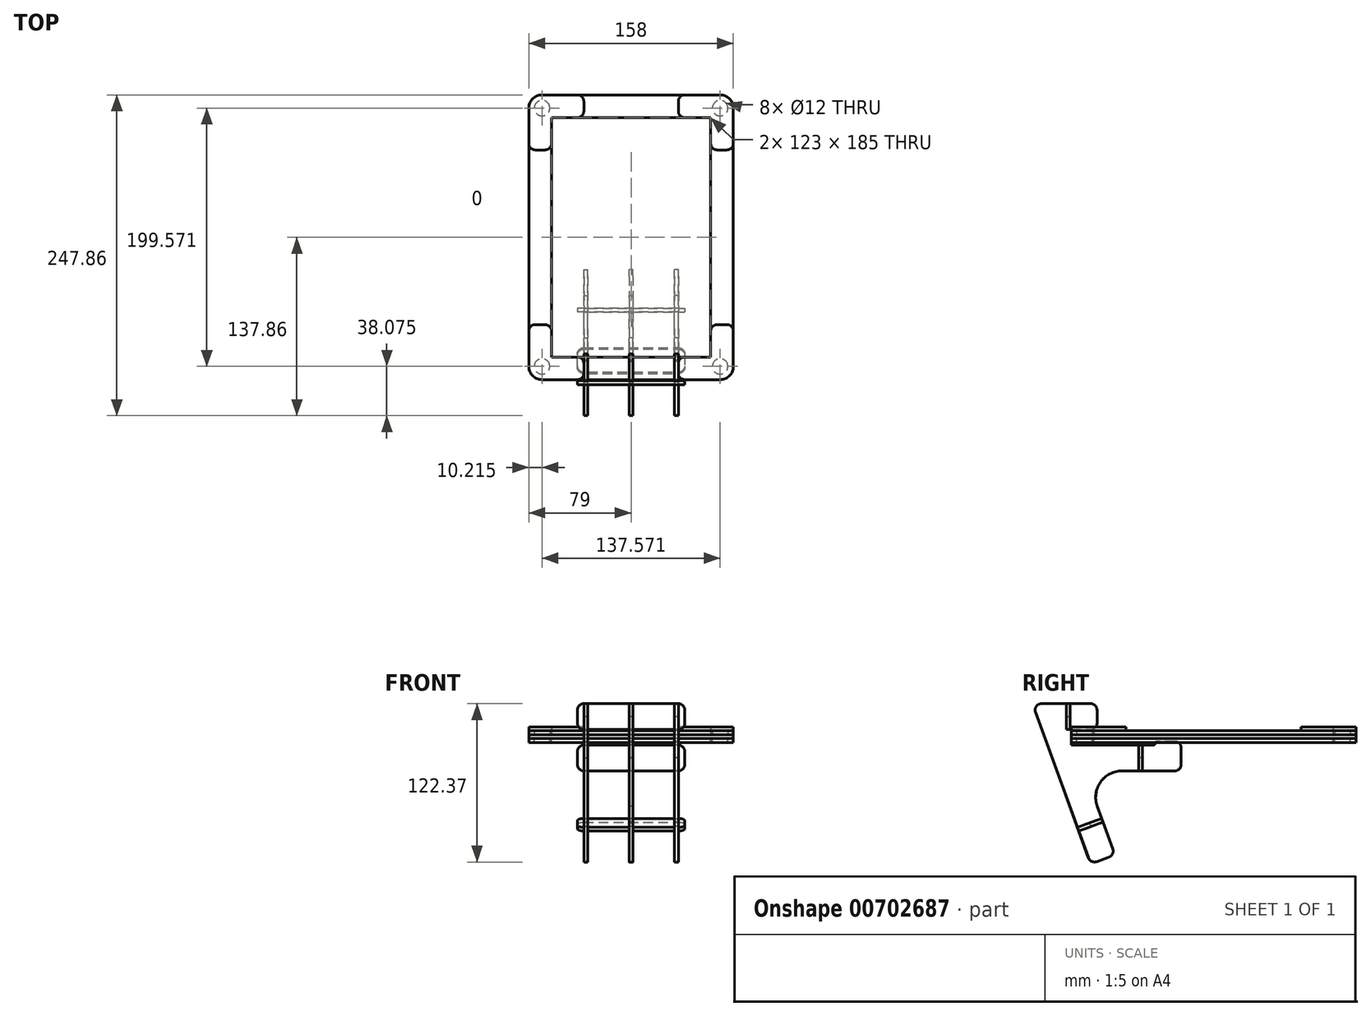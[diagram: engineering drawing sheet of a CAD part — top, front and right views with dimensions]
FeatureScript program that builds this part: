
annotation { "Feature Type Name" : "Feature", "Feature Type Description" : "" }
export const myFeature = defineFeature(function(context is Context, id is Id, definition is map)
    precondition{}
    {
        {
            var Q0;
            Q0=qCreatedBy(makeId("Top.planeOp"),FACE);
            var sketch = newSketch(context, id + "F0", { "sketchPlane" : qUnion([Q0])});
            skLineSegment(sketch, "E0.bottom", {"start": v(69, -110) * mm, "end": v(-69, -110) * mm});
            skLineSegment(sketch, "E0.top", {"start": v(69, 110) * mm, "end": v(-69, 110) * mm});
            skLineSegment(sketch, "E0.left", {"start": v(79, -100) * mm, "end": v(79, 100) * mm});
            skLineSegment(sketch, "E0.right", {"start": v(-79, -100) * mm, "end": v(-79, 100) * mm});
            skPoint(sketch, "E0.middle", {"position": v(0, 0) * mm});
            skPoint(sketch, "E1.visualSharp", {"position": v(-79, 110) * mm});
            skArc(sketch, "E1.filletArc", {"start": v(-69, 110) * mm, "mid": v(-76.07, 107.07) * mm, "end": v(-79, 100) * mm});
            skPoint(sketch, "E2.visualSharp", {"position": v(79, 110) * mm});
            skArc(sketch, "E2.filletArc", {"start": v(79, 100) * mm, "mid": v(76.07, 107.07) * mm, "end": v(69, 110) * mm});
            skPoint(sketch, "E3.visualSharp", {"position": v(79, -110) * mm});
            skArc(sketch, "E3.filletArc", {"start": v(69, -110) * mm, "mid": v(76.07, -107.07) * mm, "end": v(79, -100) * mm});
            skPoint(sketch, "E4.visualSharp", {"position": v(-79, -110) * mm});
            skArc(sketch, "E4.filletArc", {"start": v(-79, -100) * mm, "mid": v(-76.07, -107.07) * mm, "end": v(-69, -110) * mm});
            skSolve(sketch);
        }
        {
            var Q0;
            Q0 = qSketchRegion(id + "F0", true);
            extrude(context, id + "F1", {"entities" : qUnion([Q0]), "depth" : 3 * mm, "offsetDistance" : 25 * mm});
        }
        {
            var Q0;
            Q0=makeQuery(id+"F1.opExtrude","CAP_FACE",FACE,{"disambiguationData":[OSD([sQuery(id+"F0.wireOp",EDGE,"E0.bottom"),sQuery(id+"F0.wireOp",EDGE,"E0.top"),sQuery(id+"F0.wireOp",EDGE,"E0.left"),sQuery(id+"F0.wireOp",EDGE,"E0.right"),sQuery(id+"F0.wireOp",EDGE,"E1.filletArc"),sQuery(id+"F0.wireOp",EDGE,"E2.filletArc"),sQuery(id+"F0.wireOp",EDGE,"E3.filletArc"),sQuery(id+"F0.wireOp",EDGE,"E4.filletArc"),sQuery(id+"F0.wireOp",EDGE,"Dd5P2XuF-zcKf-sQkH-Ib6c-oR9rnRoDZ1EX.bottom"),sQuery(id+"F0.wireOp",EDGE,"Dd5P2XuF-zcKf-sQkH-Ib6c-oR9rnRoDZ1EX.top"),sQuery(id+"F0.wireOp",EDGE,"Dd5P2XuF-zcKf-sQkH-Ib6c-oR9rnRoDZ1EX.left"),sQuery(id+"F0.wireOp",EDGE,"Dd5P2XuF-zcKf-sQkH-Ib6c-oR9rnRoDZ1EX.right")])],"isStart":false});
            cPlane(context, id + "F2", {"entities" : qUnion([Q0]), "cplaneType" : CPlaneType.OFFSET, "offset" : 0 * mm, "width" : 150 * mm, "height" : 150 * mm});
        }
        {
            var Q0;
            Q0=qCreatedBy(id+"F2.planeOp",FACE);
            var sketch = newSketch(context, id + "F3", { "sketchPlane" : qUnion([Q0])});
            skLineSegment(sketch, "E5.bottom", {"start": v(69, -110) * mm, "end": v(-69, -110) * mm});
            skLineSegment(sketch, "E5.top", {"start": v(69, 110) * mm, "end": v(-69, 110) * mm});
            skLineSegment(sketch, "E5.left", {"start": v(79, -100) * mm, "end": v(79, 100) * mm});
            skLineSegment(sketch, "E5.right", {"start": v(-79, -100) * mm, "end": v(-79, 100) * mm});
            skPoint(sketch, "E5.middle", {"position": v(0, 0) * mm});
            skPoint(sketch, "E6.visualSharp", {"position": v(-79, 110) * mm});
            skArc(sketch, "E6.filletArc", {"start": v(-69, 110) * mm, "mid": v(-76.07, 107.07) * mm, "end": v(-79, 100) * mm});
            skPoint(sketch, "E7.visualSharp", {"position": v(79, 110) * mm});
            skArc(sketch, "E7.filletArc", {"start": v(79, 100) * mm, "mid": v(76.07, 107.07) * mm, "end": v(69, 110) * mm});
            skPoint(sketch, "E8.visualSharp", {"position": v(79, -110) * mm});
            skArc(sketch, "E8.filletArc", {"start": v(69, -110) * mm, "mid": v(76.07, -107.07) * mm, "end": v(79, -100) * mm});
            skPoint(sketch, "E9.visualSharp", {"position": v(-79, -110) * mm});
            skArc(sketch, "E9.filletArc", {"start": v(-79, -100) * mm, "mid": v(-76.07, -107.07) * mm, "end": v(-69, -110) * mm});
            skLineSegment(sketch, "E10.bottom", {"start": v(61.5, -92.5) * mm, "end": v(-61.5, -92.5) * mm});
            skLineSegment(sketch, "E10.top", {"start": v(61.5, 92.5) * mm, "end": v(-61.5, 92.5) * mm});
            skLineSegment(sketch, "E10.left", {"start": v(61.5, -92.5) * mm, "end": v(61.5, 92.5) * mm});
            skLineSegment(sketch, "E10.right", {"start": v(-61.5, -92.5) * mm, "end": v(-61.5, 92.5) * mm});
            skCircle(sketch, "E11", {"center": v(-68.79, 99.79) * mm, "radius": 6 * mm});
            skPoint(sketch, "E12.start.orphan", {"position": v(-76.07, 107.07) * mm});
            skLineSegment(sketch, "E13", {"start": v(-26.23, 0) * mm, "end": v(19.42, 0) * mm, "construction": true});
            skLineSegment(sketch, "E14", {"start": v(0, 28.6) * mm, "end": v(0, -24.47) * mm, "construction": true});
            skCircle(sketch, "E15.MirrorC", {"center": v(68.79, 99.79) * mm, "radius": 6 * mm});
            skLineSegment(sketch, "E16.MirrorCS", {"start": v(26.23, 0) * mm, "end": v(-19.42, 0) * mm, "construction": true});
            skCircle(sketch, "E17.MirrorC", {"center": v(-68.79, -99.79) * mm, "radius": 6 * mm});
            skCircle(sketch, "E18.MirrorC", {"center": v(68.79, -99.79) * mm, "radius": 6 * mm});
            skSolve(sketch);
        }
        {
            var Q0;
            Q0 = qSketchRegion(id + "F3", true);
            extrude(context, id + "F4", {"entities" : qUnion([Q0]), "depth" : 3 * mm, "offsetDistance" : 25 * mm});
        }
        {
            var Q0;
            Q0=makeQuery(id+"F1.opExtrude","CAP_FACE",FACE,{"disambiguationData":[OSD([sQuery(id+"F0.wireOp",EDGE,"E0.bottom"),sQuery(id+"F0.wireOp",EDGE,"E0.top"),sQuery(id+"F0.wireOp",EDGE,"E0.left"),sQuery(id+"F0.wireOp",EDGE,"E0.right"),sQuery(id+"F0.wireOp",EDGE,"E1.filletArc"),sQuery(id+"F0.wireOp",EDGE,"E2.filletArc"),sQuery(id+"F0.wireOp",EDGE,"E3.filletArc"),sQuery(id+"F0.wireOp",EDGE,"E4.filletArc")])],"isStart":true});
            var sketch = newSketch(context, id + "F5", { "sketchPlane" : qUnion([Q0])});
            skLineSegment(sketch, "E19.bottom", {"start": v(69, -110) * mm, "end": v(-69, -110) * mm});
            skLineSegment(sketch, "E19.top", {"start": v(69, 110) * mm, "end": v(-69, 110) * mm});
            skLineSegment(sketch, "E19.left", {"start": v(79, -100) * mm, "end": v(79, 100) * mm});
            skLineSegment(sketch, "E19.right", {"start": v(-79, -100) * mm, "end": v(-79, 100) * mm});
            skPoint(sketch, "E19.middle", {"position": v(0, 0) * mm});
            skPoint(sketch, "E20.visualSharp", {"position": v(-79, 110) * mm});
            skArc(sketch, "E20.filletArc", {"start": v(-69, 110) * mm, "mid": v(-76.07, 107.07) * mm, "end": v(-79, 100) * mm});
            skPoint(sketch, "E21.visualSharp", {"position": v(79, 110) * mm});
            skArc(sketch, "E21.filletArc", {"start": v(79, 100) * mm, "mid": v(76.07, 107.07) * mm, "end": v(69, 110) * mm});
            skPoint(sketch, "E22.visualSharp", {"position": v(79, -110) * mm});
            skArc(sketch, "E22.filletArc", {"start": v(69, -110) * mm, "mid": v(76.07, -107.07) * mm, "end": v(79, -100) * mm});
            skPoint(sketch, "E23.visualSharp", {"position": v(-79, -110) * mm});
            skArc(sketch, "E23.filletArc", {"start": v(-79, -100) * mm, "mid": v(-76.07, -107.07) * mm, "end": v(-69, -110) * mm});
            skLineSegment(sketch, "E24.bottom", {"start": v(61.5, -92.5) * mm, "end": v(-61.5, -92.5) * mm});
            skLineSegment(sketch, "E24.top", {"start": v(61.5, 92.5) * mm, "end": v(-61.5, 92.5) * mm});
            skLineSegment(sketch, "E24.left", {"start": v(61.5, -92.5) * mm, "end": v(61.5, 92.5) * mm});
            skLineSegment(sketch, "E24.right", {"start": v(-61.5, -92.5) * mm, "end": v(-61.5, 92.5) * mm});
            skLineSegment(sketch, "E25", {"start": v(0, 24.2) * mm, "end": v(0, -20.96) * mm, "construction": true});
            skLineSegment(sketch, "E26", {"start": v(-24.02, 0) * mm, "end": v(22.46, 0) * mm, "construction": true});
            skCircle(sketch, "E27", {"center": v(-68.79, 99.79) * mm, "radius": 6 * mm});
            skCircle(sketch, "E28.MirrorC", {"center": v(68.79, 99.79) * mm, "radius": 6 * mm});
            skLineSegment(sketch, "E29.MirrorCS", {"start": v(24.02, 0) * mm, "end": v(-22.46, 0) * mm, "construction": true});
            skCircle(sketch, "E30.MirrorC", {"center": v(-68.79, -99.79) * mm, "radius": 6 * mm});
            skCircle(sketch, "E31.MirrorC", {"center": v(68.79, -99.79) * mm, "radius": 6 * mm});
            skSolve(sketch);
        }
        {
            var Q0;
            Q0 = qSketchRegion(id + "F5", true);
            extrude(context, id + "F6", {"entities" : qUnion([Q0]), "depth" : 3 * mm, "offsetDistance" : 25 * mm});
        }
        {
            var Q0;
            Q0=qCreatedBy(makeId("Right.planeOp"),FACE);
            cPlane(context, id + "F7", {"entities" : qUnion([Q0]), "cplaneType" : CPlaneType.OFFSET, "offset" : 35 * mm, "width" : 150 * mm, "height" : 150 * mm});
        }
        {
            var Q0;
            Q0=qCreatedBy(id+"F7.planeOp",FACE);
            var sketch = newSketch(context, id + "F8", { "sketchPlane" : qUnion([Q0])});
            skPoint(sketch, "E32.0", {"position": v(-110, -1.5) * mm});
            skPoint(sketch, "E33.0.end.orphan", {"position": v(-110, 0) * mm});
            skPoint(sketch, "E33.0.start.orphan", {"position": v(-110, 3) * mm});
            skPoint(sketch, "E34.0.3.end.orphan", {"position": v(-100, 0) * mm});
            skPoint(sketch, "E35.0.1.start.orphan", {"position": v(-100, 3) * mm});
            skPoint(sketch, "E35.0.2.start.orphan", {"position": v(-100, 6) * mm});
            skPoint(sketch, "E34.0.2.end.orphan", {"position": v(-100, -3) * mm});
            skPoint(sketch, "E36.orphan", {"position": v(-110, 11.46) * mm});
            skPoint(sketch, "E37.end.orphan", {"position": v(-110, -3) * mm});
            skPoint(sketch, "E38.start.orphan", {"position": v(-110, 6) * mm});
            skLineSegment(sketch, "E39", {"start": v(-110, 7) * mm, "end": v(-110, -5) * mm});
            skLineSegment(sketch, "E40", {"start": v(-110, 7) * mm, "end": v(-95, 7) * mm});
            skLineSegment(sketch, "E41", {"start": v(-90, 12) * mm, "end": v(-90, 22) * mm});
            skLineSegment(sketch, "E42", {"start": v(-95, 27) * mm, "end": v(-111, 27) * mm});
            skLineSegment(sketch, "E43", {"start": v(-137.56, 20.29) * mm, "end": v(-128.92, -3.44) * mm});
            skLineSegment(sketch, "E44", {"start": v(-128.92, -3.44) * mm, "end": v(-96.66, -92.07) * mm});
            skLineSegment(sketch, "E45", {"start": v(-30, -3.5) * mm, "end": v(-30, -3.5) * mm});
            skPoint(sketch, "E46.start.orphan", {"position": v(-25, -5) * mm});
            skLineSegment(sketch, "E47", {"start": v(-25, -7) * mm, "end": v(-25, -20) * mm});
            skLineSegment(sketch, "E48", {"start": v(-30, -25) * mm, "end": v(-55, -25) * mm});
            skLineSegment(sketch, "E49", {"start": v(-89.84, -52.34) * mm, "end": v(-86.42, -61.73) * mm});
            skLineSegment(sketch, "E50", {"start": v(-80.86, -91.63) * mm, "end": v(-90.26, -95.05) * mm});
            skPoint(sketch, "E51.visualSharp", {"position": v(-140, 27) * mm});
            skArc(sketch, "E51.filletArc", {"start": v(-132.86, 27) * mm, "mid": v(-136.96, 24.87) * mm, "end": v(-137.56, 20.29) * mm});
            skPoint(sketch, "E52.visualSharp", {"position": v(-76.16, -89.92) * mm});
            skArc(sketch, "E52.filletArc", {"start": v(-80.86, -91.63) * mm, "mid": v(-78.04, -89.05) * mm, "end": v(-77.87, -85.23) * mm});
            skPoint(sketch, "E53.visualSharp", {"position": v(-90, 27) * mm});
            skArc(sketch, "E53.filletArc", {"start": v(-90, 22) * mm, "mid": v(-91.46, 25.54) * mm, "end": v(-95, 27) * mm});
            skPoint(sketch, "E54.visualSharp", {"position": v(-90, 7) * mm});
            skArc(sketch, "E54.filletArc", {"start": v(-95, 7) * mm, "mid": v(-91.46, 8.46) * mm, "end": v(-90, 12) * mm});
            skPoint(sketch, "E55.visualSharp", {"position": v(-94.95, -96.76) * mm});
            skArc(sketch, "E55.filletArc", {"start": v(-96.66, -92.07) * mm, "mid": v(-94.08, -94.89) * mm, "end": v(-90.26, -95.05) * mm});
            skArc(sketch, "E56.filletArc", {"start": v(-70.7, -25) * mm, "mid": v(-87.39, -33.69) * mm, "end": v(-89.84, -52.34) * mm});
            skPoint(sketch, "E57.visualSharp", {"position": v(-25, -2) * mm});
            skArc(sketch, "E57.filletArc", {"start": v(-25, -7) * mm, "mid": v(-26.46, -3.46) * mm, "end": v(-30, -2) * mm});
            skPoint(sketch, "E58.visualSharp", {"position": v(-25, -25) * mm});
            skArc(sketch, "E58.filletArc", {"start": v(-30, -25) * mm, "mid": v(-26.46, -23.54) * mm, "end": v(-25, -20) * mm});
            skPoint(sketch, "E59.visualSharp", {"position": v(-45, -2) * mm});
            skArc(sketch, "E59.filletArc", {"start": v(-43.5, -2) * mm, "mid": v(-44.56, -2.44) * mm, "end": v(-45, -3.5) * mm});
            skPoint(sketch, "E60.visualSharp", {"position": v(-45, -5) * mm});
            skArc(sketch, "E60.filletArc", {"start": v(-46.5, -5) * mm, "mid": v(-45.44, -4.56) * mm, "end": v(-45, -3.5) * mm});
            skLineSegment(sketch, "E61", {"start": v(-86.42, -61.73) * mm, "end": v(-95.82, -65.15) * mm});
            skLineSegment(sketch, "E62", {"start": v(-95.82, -65.15) * mm, "end": v(-94.86, -67.78) * mm});
            skLineSegment(sketch, "E63", {"start": v(-94.86, -67.78) * mm, "end": v(-85.46, -64.36) * mm});
            skLineSegment(sketch, "E64.trimOffspring", {"start": v(-85.46, -64.36) * mm, "end": v(-77.87, -85.23) * mm});
            skLineSegment(sketch, "E65", {"start": v(-55, -25) * mm, "end": v(-55, -15) * mm});
            skLineSegment(sketch, "E66", {"start": v(-55, -15) * mm, "end": v(-57.8, -15) * mm});
            skLineSegment(sketch, "E67", {"start": v(-57.8, -15) * mm, "end": v(-57.8, -25) * mm});
            skLineSegment(sketch, "E68", {"start": v(-113.8, 27) * mm, "end": v(-113.8, 17) * mm});
            skLineSegment(sketch, "E69", {"start": v(-113.8, 17) * mm, "end": v(-111, 17) * mm});
            skLineSegment(sketch, "E70", {"start": v(-111, 17) * mm, "end": v(-111, 27) * mm});
            skLineSegment(sketch, "E71.trimOffspring", {"start": v(-113.8, 27) * mm, "end": v(-132.86, 27) * mm});
            skLineSegment(sketch, "E72", {"start": v(-110, -5) * mm, "end": v(-46.5, -5) * mm});
            skLineSegment(sketch, "E73", {"start": v(-43.5, -2) * mm, "end": v(-30, -2) * mm});
            skLineSegment(sketch, "E74", {"start": v(-70.7, -25) * mm, "end": v(-57.8, -25) * mm});
            skSolve(sketch);
        }
        {
            var Q0;
            Q0 = qSketchRegion(id + "F8", true);
            extrude(context, id + "F9", {"entities" : qUnion([Q0]), "endBound" : BoundingType.SYMMETRIC, "depth" : 3 * mm, "offsetDistance" : 25 * mm});
        }
        {
            var Q0;
            Q0=qCreatedBy(makeId("Right.planeOp"),FACE);
            var sketch = newSketch(context, id + "F10", { "sketchPlane" : qUnion([Q0])});
            skPoint(sketch, "E75.0", {"position": v(-110.75, -5.36) * mm});
            skPoint(sketch, "E76.0.end.orphan", {"position": v(-110.75, -3.86) * mm});
            skPoint(sketch, "E76.0.start.orphan", {"position": v(-110.75, -0.86) * mm});
            skPoint(sketch, "E77.0.3.end.orphan", {"position": v(-100.75, -3.86) * mm});
            skPoint(sketch, "E78.0.1.start.orphan", {"position": v(-100.75, -0.86) * mm});
            skPoint(sketch, "E78.0.2.start.orphan", {"position": v(-100.75, 2.14) * mm});
            skPoint(sketch, "E77.0.2.end.orphan", {"position": v(-100.75, -6.86) * mm});
            skPoint(sketch, "E79.orphan", {"position": v(-110.75, 7.6) * mm});
            skPoint(sketch, "E80.end.orphan", {"position": v(-110.75, -6.86) * mm});
            skPoint(sketch, "E81.start.orphan", {"position": v(-110.75, 2.14) * mm});
            skLineSegment(sketch, "E82", {"start": v(-110.75, 3.14) * mm, "end": v(-110.75, -8.86) * mm});
            skLineSegment(sketch, "E83", {"start": v(-110.75, 3.14) * mm, "end": v(-95.75, 3.14) * mm});
            skLineSegment(sketch, "E84", {"start": v(-90.75, 8.14) * mm, "end": v(-90.75, 18.14) * mm});
            skLineSegment(sketch, "E85", {"start": v(-95.75, 23.14) * mm, "end": v(-111.75, 23.14) * mm});
            skLineSegment(sketch, "E86", {"start": v(-138.31, 16.43) * mm, "end": v(-129.67, -7.3) * mm});
            skLineSegment(sketch, "E87", {"start": v(-30.75, -5.86) * mm, "end": v(-44.25, -5.86) * mm});
            skLineSegment(sketch, "E88", {"start": v(-15.58, -62.05) * mm, "end": v(-15.58, -62.05) * mm});
            skLineSegment(sketch, "E89", {"start": v(-36.7, -63.55) * mm, "end": v(-36.7, -63.55) * mm});
            skPoint(sketch, "E90.start.orphan", {"position": v(-25.75, -8.86) * mm});
            skLineSegment(sketch, "E91", {"start": v(-25.75, -10.86) * mm, "end": v(-25.75, -23.86) * mm});
            skLineSegment(sketch, "E92", {"start": v(-30.75, -28.86) * mm, "end": v(-55.75, -28.86) * mm});
            skLineSegment(sketch, "E93", {"start": v(-81.72, -95.45) * mm, "end": v(-91.1, -98.92) * mm});
            skPoint(sketch, "E94.visualSharp", {"position": v(-140.75, 23.14) * mm});
            skArc(sketch, "E94.filletArc", {"start": v(-133.61, 23.14) * mm, "mid": v(-137.7, 21) * mm, "end": v(-138.31, 16.43) * mm});
            skPoint(sketch, "E95.visualSharp", {"position": v(-77.03, -93.71) * mm});
            skArc(sketch, "E95.filletArc", {"start": v(-81.72, -95.45) * mm, "mid": v(-78.91, -92.85) * mm, "end": v(-78.77, -89.02) * mm});
            skPoint(sketch, "E96.visualSharp", {"position": v(-90.75, 23.14) * mm});
            skArc(sketch, "E96.filletArc", {"start": v(-90.75, 18.14) * mm, "mid": v(-92.22, 21.67) * mm, "end": v(-95.75, 23.14) * mm});
            skPoint(sketch, "E97.visualSharp", {"position": v(-90.75, 3.14) * mm});
            skArc(sketch, "E97.filletArc", {"start": v(-95.75, 3.14) * mm, "mid": v(-92.22, 4.6) * mm, "end": v(-90.75, 8.14) * mm});
            skPoint(sketch, "E98.visualSharp", {"position": v(-95.78, -100.66) * mm});
            skArc(sketch, "E98.filletArc", {"start": v(-97.52, -95.97) * mm, "mid": v(-94.92, -98.78) * mm, "end": v(-91.1, -98.92) * mm});
            skArc(sketch, "E99.filletArc", {"start": v(-71.45, -28.86) * mm, "mid": v(-88.14, -37.55) * mm, "end": v(-90.6, -56.2) * mm});
            skPoint(sketch, "E100.visualSharp", {"position": v(-25.75, -5.86) * mm});
            skArc(sketch, "E100.filletArc", {"start": v(-25.75, -10.86) * mm, "mid": v(-27.22, -7.33) * mm, "end": v(-30.75, -5.86) * mm});
            skPoint(sketch, "E101.visualSharp", {"position": v(-25.75, -28.86) * mm});
            skArc(sketch, "E101.filletArc", {"start": v(-30.75, -28.86) * mm, "mid": v(-27.22, -27.4) * mm, "end": v(-25.75, -23.86) * mm});
            skPoint(sketch, "E102.visualSharp", {"position": v(-45.75, -5.86) * mm});
            skArc(sketch, "E102.filletArc", {"start": v(-44.25, -5.86) * mm, "mid": v(-45.31, -6.3) * mm, "end": v(-45.75, -7.36) * mm});
            skPoint(sketch, "E103.visualSharp", {"position": v(-45.75, -8.86) * mm});
            skArc(sketch, "E103.filletArc", {"start": v(-47.25, -8.86) * mm, "mid": v(-46.2, -8.42) * mm, "end": v(-45.75, -7.36) * mm});
            skLineSegment(sketch, "E104", {"start": v(-87.45, -65.58) * mm, "end": v(-96.83, -69.05) * mm});
            skLineSegment(sketch, "E105", {"start": v(-96.83, -69.05) * mm, "end": v(-95.85, -71.68) * mm});
            skLineSegment(sketch, "E106", {"start": v(-95.85, -71.68) * mm, "end": v(-86.48, -68.2) * mm});
            skLineSegment(sketch, "E107.trimOffspring", {"start": v(-86.48, -68.2) * mm, "end": v(-78.77, -89.02) * mm});
            skLineSegment(sketch, "E108", {"start": v(-55.75, -28.86) * mm, "end": v(-55.75, -18.86) * mm});
            skLineSegment(sketch, "E109", {"start": v(-55.75, -18.86) * mm, "end": v(-58.55, -18.86) * mm});
            skLineSegment(sketch, "E110", {"start": v(-58.55, -18.86) * mm, "end": v(-58.55, -28.86) * mm});
            skLineSegment(sketch, "E111", {"start": v(-114.55, 23.14) * mm, "end": v(-114.55, 13.14) * mm});
            skLineSegment(sketch, "E112", {"start": v(-114.55, 13.14) * mm, "end": v(-111.75, 13.14) * mm});
            skLineSegment(sketch, "E113", {"start": v(-111.75, 13.14) * mm, "end": v(-111.75, 23.14) * mm});
            skLineSegment(sketch, "E114.trimOffspring", {"start": v(-114.55, 23.14) * mm, "end": v(-133.61, 23.14) * mm});
            skLineSegment(sketch, "E115", {"start": v(-71.45, -28.86) * mm, "end": v(-58.55, -28.86) * mm});
            skLineSegment(sketch, "E116", {"start": v(-47.25, -8.86) * mm, "end": v(-110.75, -8.86) * mm});
            skLineSegment(sketch, "E117", {"start": v(-97.52, -95.97) * mm, "end": v(-129.67, -7.3) * mm});
            skLineSegment(sketch, "E118", {"start": v(-90.6, -56.2) * mm, "end": v(-87.45, -65.58) * mm});
            skSolve(sketch);
        }
        {
            var Q0;
            Q0 = qSketchRegion(id + "F10", true);
            extrude(context, id + "F11", {"entities" : qUnion([Q0]), "endBound" : BoundingType.SYMMETRIC, "depth" : 3 * mm, "offsetDistance" : 25 * mm});
        }
        {
            var Q0;
            Q0=makeQuery(id+"F11.opExtrude","SWEPT_BODY",BODY,{"disambiguationData":[OSD([sQuery(id+"F10.wireOp",EDGE,"E82"),sQuery(id+"F10.wireOp",EDGE,"E83"),sQuery(id+"F10.wireOp",EDGE,"E84"),sQuery(id+"F10.wireOp",EDGE,"E85"),sQuery(id+"F10.wireOp",EDGE,"E86"),sQuery(id+"F10.wireOp",EDGE,"bd648344-6ee6-407b-a3d3-1d98c72f2c9b"),sQuery(id+"F10.wireOp",EDGE,"ca2a9264-c919-42b0-badf-f22fe449a8f8"),sQuery(id+"F10.wireOp",EDGE,"E87"),sQuery(id+"F10.wireOp",EDGE,"E91"),sQuery(id+"F10.wireOp",EDGE,"E92"),sQuery(id+"F10.wireOp",EDGE,"bc421cfa-79b9-4f05-873c-a9f864f837b1"),sQuery(id+"F10.wireOp",EDGE,"E93"),sQuery(id+"F10.wireOp",EDGE,"E94.filletArc"),sQuery(id+"F10.wireOp",EDGE,"E95.filletArc"),sQuery(id+"F10.wireOp",EDGE,"E96.filletArc"),sQuery(id+"F10.wireOp",EDGE,"E97.filletArc"),sQuery(id+"F10.wireOp",EDGE,"E98.filletArc"),sQuery(id+"F10.wireOp",EDGE,"E99.filletArc"),sQuery(id+"F10.wireOp",EDGE,"E100.filletArc"),sQuery(id+"F10.wireOp",EDGE,"E101.filletArc"),sQuery(id+"F10.wireOp",EDGE,"E102.filletArc"),sQuery(id+"F10.wireOp",EDGE,"E103.filletArc"),sQuery(id+"F10.wireOp",EDGE,"E104"),sQuery(id+"F10.wireOp",EDGE,"E105"),sQuery(id+"F10.wireOp",EDGE,"E106"),sQuery(id+"F10.wireOp",EDGE,"E107.trimOffspring"),sQuery(id+"F10.wireOp",EDGE,"E108"),sQuery(id+"F10.wireOp",EDGE,"E109"),sQuery(id+"F10.wireOp",EDGE,"E110"),sQuery(id+"F10.wireOp",EDGE,"9e8f19d4-f606-473f-a8e4-5bbb00c72346.trimOffspring")])]});
            transform(context, id + "F12", {"entities" : qUnion([Q0]), "transformType" : TransformType.TRANSLATION_3D, "dx" : 0 * mm, "dy" : 0 * mm, "dz" : 4 * mm, "makeCopy" : false});
        }
        {
            var Q0;
            Q0=makeQuery(id+"F9.opExtrude","SWEPT_BODY",BODY,{"disambiguationData":[OSD([sQuery(id+"F8.wireOp",EDGE,"E39"),sQuery(id+"F8.wireOp",EDGE,"E40"),sQuery(id+"F8.wireOp",EDGE,"E41"),sQuery(id+"F8.wireOp",EDGE,"E42"),sQuery(id+"F8.wireOp",EDGE,"E43"),sQuery(id+"F8.wireOp",EDGE,"E44"),sQuery(id+"F8.wireOp",EDGE,"Sl3nM0fF-2x2T-EpRs-04C0-HyGomDlCLGSy"),sQuery(id+"F8.wireOp",EDGE,"FvY40X7a-xvkL-cqhL-q3nA-5QotTi6xHMw6"),sQuery(id+"F8.wireOp",EDGE,"E47"),sQuery(id+"F8.wireOp",EDGE,"E48"),sQuery(id+"F8.wireOp",EDGE,"E49"),sQuery(id+"F8.wireOp",EDGE,"E50"),sQuery(id+"F8.wireOp",EDGE,"E51.filletArc"),sQuery(id+"F8.wireOp",EDGE,"E52.filletArc"),sQuery(id+"F8.wireOp",EDGE,"E53.filletArc"),sQuery(id+"F8.wireOp",EDGE,"E54.filletArc"),sQuery(id+"F8.wireOp",EDGE,"E55.filletArc"),sQuery(id+"F8.wireOp",EDGE,"E56.filletArc"),sQuery(id+"F8.wireOp",EDGE,"E57.filletArc"),sQuery(id+"F8.wireOp",EDGE,"E58.filletArc"),sQuery(id+"F8.wireOp",EDGE,"E59.filletArc"),sQuery(id+"F8.wireOp",EDGE,"E60.filletArc"),sQuery(id+"F8.wireOp",EDGE,"E61"),sQuery(id+"F8.wireOp",EDGE,"E62"),sQuery(id+"F8.wireOp",EDGE,"E63"),sQuery(id+"F8.wireOp",EDGE,"E64.trimOffspring"),sQuery(id+"F8.wireOp",EDGE,"E65"),sQuery(id+"F8.wireOp",EDGE,"E66"),sQuery(id+"F8.wireOp",EDGE,"E67"),sQuery(id+"F8.wireOp",EDGE,"eae0e394-da7d-408e-a25a-b20038e35a28.trimOffspring")])]});
            var Q1;
            Q1=qCreatedBy(makeId("Right.planeOp"),FACE);
            mirror(context, id + "F13", {"entities" : qUnion([Q0]), "mirrorPlane" : qUnion([Q1])});
        }
        {
            var Q0;
            Q0=makeQuery(id+"F13.opPattern","COPY",FACE,{"derivedFrom":makeQuery(id+"F9.opExtrude","SWEPT_FACE",FACE,{"disambiguationData":[OSD([sQuery(id+"F8.wireOp",EDGE,"E68")])]}),"instanceName":"1"});
            cPlane(context, id + "F14", {"entities" : qUnion([Q0]), "cplaneType" : CPlaneType.OFFSET, "offset" : 0 * mm, "width" : 150 * mm, "height" : 150 * mm});
        }
        {
            var Q0;
            Q0=qCreatedBy(id+"F14.planeOp",FACE);
            var sketch = newSketch(context, id + "F15", { "sketchPlane" : qUnion([Q0])});
            skLineSegment(sketch, "E119.0.3", {"start": v(-1.5, 17) * mm, "end": v(1.5, 17) * mm});
            skLineSegment(sketch, "E120", {"start": v(-41.5, 22) * mm, "end": v(-41.5, 12) * mm});
            skLineSegment(sketch, "E121", {"start": v(41.5, 12) * mm, "end": v(41.5, 22) * mm});
            skPoint(sketch, "E122.visualSharp", {"position": v(-41.5, 27) * mm});
            skArc(sketch, "E122.filletArc", {"start": v(-36.5, 27) * mm, "mid": v(-40.04, 25.54) * mm, "end": v(-41.5, 22) * mm});
            skPoint(sketch, "E123.visualSharp", {"position": v(-41.5, 7) * mm});
            skArc(sketch, "E123.filletArc", {"start": v(-41.5, 12) * mm, "mid": v(-40.04, 8.46) * mm, "end": v(-36.5, 7) * mm});
            skPoint(sketch, "E124.visualSharp", {"position": v(41.5, 27) * mm});
            skArc(sketch, "E124.filletArc", {"start": v(41.5, 22) * mm, "mid": v(40.04, 25.54) * mm, "end": v(36.5, 27) * mm});
            skPoint(sketch, "E125.visualSharp", {"position": v(41.5, 7) * mm});
            skArc(sketch, "E125.filletArc", {"start": v(36.5, 7) * mm, "mid": v(40.04, 8.46) * mm, "end": v(41.5, 12) * mm});
            skLineSegment(sketch, "E126.MirrorCS", {"start": v(33.5, 7) * mm, "end": v(33.5, 17) * mm});
            skLineSegment(sketch, "E127.MirrorCS", {"start": v(36.5, 17) * mm, "end": v(36.5, 7) * mm});
            skLineSegment(sketch, "E128.MirrorCS", {"start": v(33.5, 17) * mm, "end": v(36.5, 17) * mm});
            skLineSegment(sketch, "E129.MirrorCS", {"start": v(-33.5, 17) * mm, "end": v(-33.5, 7) * mm});
            skLineSegment(sketch, "E130.MirrorCS", {"start": v(-36.5, 17) * mm, "end": v(-33.5, 17) * mm});
            skLineSegment(sketch, "E131.MirrorCS", {"start": v(-36.5, 7) * mm, "end": v(-36.5, 17) * mm});
            skLineSegment(sketch, "E132.MirrorCS", {"start": v(1.5, 17) * mm, "end": v(1.5, 7) * mm});
            skLineSegment(sketch, "E133.MirrorCS", {"start": v(-1.5, 7) * mm, "end": v(-1.5, 17) * mm});
            skPoint(sketch, "E134.0", {"position": v(33.5, 17) * mm});
            skPoint(sketch, "E135.0", {"position": v(-36.5, 17) * mm});
            skPoint(sketch, "E136.orphan", {"position": v(36.5, 27) * mm});
            skPoint(sketch, "E137.end.orphan", {"position": v(-36.5, 27) * mm});
            skLineSegment(sketch, "E138", {"start": v(36.5, 27) * mm, "end": v(-36.5, 27) * mm});
            skLineSegment(sketch, "E139", {"start": v(33.5, 7) * mm, "end": v(1.5, 7) * mm});
            skLineSegment(sketch, "E140", {"start": v(-1.5, 7) * mm, "end": v(-33.5, 7) * mm});
            skSolve(sketch);
        }
        {
            var Q0;
            Q0=makeQuery(id+"F11.opExtrude","SWEPT_BODY",BODY,{"disambiguationData":[OSD([sQuery(id+"F10.wireOp",EDGE,"E82"),sQuery(id+"F10.wireOp",EDGE,"E83"),sQuery(id+"F10.wireOp",EDGE,"E84"),sQuery(id+"F10.wireOp",EDGE,"E85"),sQuery(id+"F10.wireOp",EDGE,"E86"),sQuery(id+"F10.wireOp",EDGE,"bd648344-6ee6-407b-a3d3-1d98c72f2c9b"),sQuery(id+"F10.wireOp",EDGE,"ca2a9264-c919-42b0-badf-f22fe449a8f8"),sQuery(id+"F10.wireOp",EDGE,"E87"),sQuery(id+"F10.wireOp",EDGE,"E91"),sQuery(id+"F10.wireOp",EDGE,"E92"),sQuery(id+"F10.wireOp",EDGE,"bc421cfa-79b9-4f05-873c-a9f864f837b1"),sQuery(id+"F10.wireOp",EDGE,"E93"),sQuery(id+"F10.wireOp",EDGE,"E94.filletArc"),sQuery(id+"F10.wireOp",EDGE,"E95.filletArc"),sQuery(id+"F10.wireOp",EDGE,"E96.filletArc"),sQuery(id+"F10.wireOp",EDGE,"E97.filletArc"),sQuery(id+"F10.wireOp",EDGE,"E98.filletArc"),sQuery(id+"F10.wireOp",EDGE,"E99.filletArc"),sQuery(id+"F10.wireOp",EDGE,"E100.filletArc"),sQuery(id+"F10.wireOp",EDGE,"E101.filletArc"),sQuery(id+"F10.wireOp",EDGE,"E102.filletArc"),sQuery(id+"F10.wireOp",EDGE,"E103.filletArc"),sQuery(id+"F10.wireOp",EDGE,"E104"),sQuery(id+"F10.wireOp",EDGE,"E105"),sQuery(id+"F10.wireOp",EDGE,"E106"),sQuery(id+"F10.wireOp",EDGE,"E107.trimOffspring"),sQuery(id+"F10.wireOp",EDGE,"E108"),sQuery(id+"F10.wireOp",EDGE,"E109"),sQuery(id+"F10.wireOp",EDGE,"E110"),sQuery(id+"F10.wireOp",EDGE,"9e8f19d4-f606-473f-a8e4-5bbb00c72346.trimOffspring"),sQuery(id+"F10.wireOp",EDGE,"E111"),sQuery(id+"F10.wireOp",EDGE,"E112"),sQuery(id+"F10.wireOp",EDGE,"E113"),sQuery(id+"F10.wireOp",EDGE,"E114.trimOffspring")])]});
            transform(context, id + "F16", {"entities" : qUnion([Q0]), "transformType" : TransformType.TRANSLATION_3D, "dx" : 0 * mm, "dy" : 0 * mm, "dz" : 0.14 * mm, "makeCopy" : false});
        }
        {
            var Q0;
            Q0 = qSketchRegion(id + "F15", true);
            extrude(context, id + "F17", {"entities" : qUnion([Q0]), "depth" : 3 * mm, "offsetDistance" : 25 * mm});
        }
        {
            var Q0;
            Q0=makeQuery(id+"F11.opExtrude","SWEPT_BODY",BODY,{"disambiguationData":[OSD([sQuery(id+"F10.wireOp",EDGE,"E82"),sQuery(id+"F10.wireOp",EDGE,"E83"),sQuery(id+"F10.wireOp",EDGE,"E84"),sQuery(id+"F10.wireOp",EDGE,"E85"),sQuery(id+"F10.wireOp",EDGE,"E86"),sQuery(id+"F10.wireOp",EDGE,"bd648344-6ee6-407b-a3d3-1d98c72f2c9b"),sQuery(id+"F10.wireOp",EDGE,"ca2a9264-c919-42b0-badf-f22fe449a8f8"),sQuery(id+"F10.wireOp",EDGE,"E87"),sQuery(id+"F10.wireOp",EDGE,"E91"),sQuery(id+"F10.wireOp",EDGE,"E92"),sQuery(id+"F10.wireOp",EDGE,"bc421cfa-79b9-4f05-873c-a9f864f837b1"),sQuery(id+"F10.wireOp",EDGE,"E93"),sQuery(id+"F10.wireOp",EDGE,"E94.filletArc"),sQuery(id+"F10.wireOp",EDGE,"E95.filletArc"),sQuery(id+"F10.wireOp",EDGE,"E96.filletArc"),sQuery(id+"F10.wireOp",EDGE,"E97.filletArc"),sQuery(id+"F10.wireOp",EDGE,"E98.filletArc"),sQuery(id+"F10.wireOp",EDGE,"E99.filletArc"),sQuery(id+"F10.wireOp",EDGE,"E100.filletArc"),sQuery(id+"F10.wireOp",EDGE,"E101.filletArc"),sQuery(id+"F10.wireOp",EDGE,"E102.filletArc"),sQuery(id+"F10.wireOp",EDGE,"E103.filletArc"),sQuery(id+"F10.wireOp",EDGE,"E104"),sQuery(id+"F10.wireOp",EDGE,"E105"),sQuery(id+"F10.wireOp",EDGE,"E106"),sQuery(id+"F10.wireOp",EDGE,"E107.trimOffspring"),sQuery(id+"F10.wireOp",EDGE,"E108"),sQuery(id+"F10.wireOp",EDGE,"E109"),sQuery(id+"F10.wireOp",EDGE,"E110"),sQuery(id+"F10.wireOp",EDGE,"9e8f19d4-f606-473f-a8e4-5bbb00c72346.trimOffspring"),sQuery(id+"F10.wireOp",EDGE,"E111"),sQuery(id+"F10.wireOp",EDGE,"E112"),sQuery(id+"F10.wireOp",EDGE,"E113"),sQuery(id+"F10.wireOp",EDGE,"E114.trimOffspring")])]});
            transform(context, id + "F18", {"entities" : qUnion([Q0]), "transformType" : TransformType.TRANSLATION_3D, "dx" : 0 * mm, "dy" : 0.2 * mm, "dz" : -0.27 * mm, "makeCopy" : false});
        }
        {
            var Q0;
            Q0=makeQuery(id+"F11.opExtrude","SWEPT_BODY",BODY,{"disambiguationData":[OSD([sQuery(id+"F10.wireOp",EDGE,"E82"),sQuery(id+"F10.wireOp",EDGE,"E83"),sQuery(id+"F10.wireOp",EDGE,"E84"),sQuery(id+"F10.wireOp",EDGE,"E85"),sQuery(id+"F10.wireOp",EDGE,"E86"),sQuery(id+"F10.wireOp",EDGE,"bd648344-6ee6-407b-a3d3-1d98c72f2c9b"),sQuery(id+"F10.wireOp",EDGE,"ca2a9264-c919-42b0-badf-f22fe449a8f8"),sQuery(id+"F10.wireOp",EDGE,"E87"),sQuery(id+"F10.wireOp",EDGE,"E91"),sQuery(id+"F10.wireOp",EDGE,"E92"),sQuery(id+"F10.wireOp",EDGE,"bc421cfa-79b9-4f05-873c-a9f864f837b1"),sQuery(id+"F10.wireOp",EDGE,"E93"),sQuery(id+"F10.wireOp",EDGE,"E94.filletArc"),sQuery(id+"F10.wireOp",EDGE,"E95.filletArc"),sQuery(id+"F10.wireOp",EDGE,"E96.filletArc"),sQuery(id+"F10.wireOp",EDGE,"E97.filletArc"),sQuery(id+"F10.wireOp",EDGE,"E98.filletArc"),sQuery(id+"F10.wireOp",EDGE,"E99.filletArc"),sQuery(id+"F10.wireOp",EDGE,"E100.filletArc"),sQuery(id+"F10.wireOp",EDGE,"E101.filletArc"),sQuery(id+"F10.wireOp",EDGE,"E102.filletArc"),sQuery(id+"F10.wireOp",EDGE,"E103.filletArc"),sQuery(id+"F10.wireOp",EDGE,"E104"),sQuery(id+"F10.wireOp",EDGE,"E105"),sQuery(id+"F10.wireOp",EDGE,"E106"),sQuery(id+"F10.wireOp",EDGE,"E107.trimOffspring"),sQuery(id+"F10.wireOp",EDGE,"E108"),sQuery(id+"F10.wireOp",EDGE,"E109"),sQuery(id+"F10.wireOp",EDGE,"E110"),sQuery(id+"F10.wireOp",EDGE,"9e8f19d4-f606-473f-a8e4-5bbb00c72346.trimOffspring"),sQuery(id+"F10.wireOp",EDGE,"E111"),sQuery(id+"F10.wireOp",EDGE,"E112"),sQuery(id+"F10.wireOp",EDGE,"E113"),sQuery(id+"F10.wireOp",EDGE,"E114.trimOffspring")])]});
            transform(context, id + "F19", {"entities" : qUnion([Q0]), "transformType" : TransformType.TRANSLATION_3D, "dx" : 0 * mm, "dy" : 0.6 * mm, "dz" : 0 * mm, "makeCopy" : false});
        }
        {
            var Q0;
            Q0=makeQuery(id+"F9.opExtrude","SWEPT_FACE",FACE,{"disambiguationData":[OSD([sQuery(id+"F8.wireOp",EDGE,"E61")])]});
            cPlane(context, id + "F20", {"entities" : qUnion([Q0]), "cplaneType" : CPlaneType.OFFSET, "offset" : 0 * mm, "width" : 150 * mm, "height" : 150 * mm});
        }
        {
            var Q0;
            Q0=qCreatedBy(id+"F20.planeOp",FACE);
            var sketch = newSketch(context, id + "F21", { "sketchPlane" : qUnion([Q0])});
            skLineSegment(sketch, "E141", {"start": v(-88.41, 125.52) * mm, "end": v(-88.41, 125.52) * mm});
            skLineSegment(sketch, "E142.0.3", {"start": v(1.5, 112.32) * mm, "end": v(-1.5, 112.32) * mm});
            skLineSegment(sketch, "E143", {"start": v(41.5, 107.32) * mm, "end": v(41.5, 117.32) * mm});
            skLineSegment(sketch, "E144", {"start": v(-41.5, 117.32) * mm, "end": v(-41.5, 107.32) * mm});
            skPoint(sketch, "E145.visualSharp", {"position": v(41.5, 102.32) * mm});
            skArc(sketch, "E145.filletArc", {"start": v(36.5, 102.32) * mm, "mid": v(40.04, 103.79) * mm, "end": v(41.5, 107.32) * mm});
            skPoint(sketch, "E146.visualSharp", {"position": v(41.5, 122.32) * mm});
            skArc(sketch, "E146.filletArc", {"start": v(41.5, 117.32) * mm, "mid": v(40.04, 120.86) * mm, "end": v(36.5, 122.32) * mm});
            skPoint(sketch, "E147.visualSharp", {"position": v(-41.5, 102.32) * mm});
            skArc(sketch, "E147.filletArc", {"start": v(-41.5, 107.32) * mm, "mid": v(-40.04, 103.79) * mm, "end": v(-36.5, 102.32) * mm});
            skPoint(sketch, "E148.visualSharp", {"position": v(-41.5, 122.32) * mm});
            skArc(sketch, "E148.filletArc", {"start": v(-36.5, 122.32) * mm, "mid": v(-40.04, 120.86) * mm, "end": v(-41.5, 117.32) * mm});
            skLineSegment(sketch, "E149.MirrorCS", {"start": v(-33.5, 122.32) * mm, "end": v(-33.5, 112.32) * mm});
            skLineSegment(sketch, "E150.MirrorCS", {"start": v(-36.5, 112.32) * mm, "end": v(-36.5, 122.32) * mm});
            skLineSegment(sketch, "E151.MirrorCS", {"start": v(-33.5, 112.32) * mm, "end": v(-36.5, 112.32) * mm});
            skLineSegment(sketch, "E152.MirrorCS", {"start": v(33.5, 112.32) * mm, "end": v(33.5, 122.32) * mm});
            skLineSegment(sketch, "E153.MirrorCS", {"start": v(36.5, 112.32) * mm, "end": v(33.5, 112.32) * mm});
            skLineSegment(sketch, "E154.MirrorCS", {"start": v(36.5, 122.32) * mm, "end": v(36.5, 112.32) * mm});
            skLineSegment(sketch, "E155.MirrorCS", {"start": v(-1.5, 112.32) * mm, "end": v(-1.5, 122.32) * mm});
            skLineSegment(sketch, "E156.MirrorCS", {"start": v(1.5, 122.32) * mm, "end": v(1.5, 112.32) * mm});
            skPoint(sketch, "E157.0", {"position": v(-33.5, 112.32) * mm});
            skPoint(sketch, "E158.0", {"position": v(36.5, 112.32) * mm});
            skPoint(sketch, "E159.orphan", {"position": v(-36.5, 102.32) * mm});
            skPoint(sketch, "E160.end.orphan", {"position": v(36.5, 102.32) * mm});
            skLineSegment(sketch, "E161", {"start": v(-36.5, 102.32) * mm, "end": v(36.5, 102.32) * mm});
            skLineSegment(sketch, "E162", {"start": v(-33.5, 122.32) * mm, "end": v(-1.5, 122.32) * mm});
            skLineSegment(sketch, "E163", {"start": v(1.5, 122.32) * mm, "end": v(33.5, 122.32) * mm});
            skSolve(sketch);
        }
        {
            var Q0;
            Q0 = qSketchRegion(id + "F21", true);
            extrude(context, id + "F22", {"entities" : qUnion([Q0]), "depth" : 3 * mm, "offsetDistance" : 25 * mm});
        }
        {
            var Q0;
            Q0=makeQuery(id+"F9.opExtrude","SWEPT_FACE",FACE,{"disambiguationData":[OSD([sQuery(id+"F8.wireOp",EDGE,"E67")])]});
            cPlane(context, id + "F23", {"entities" : qUnion([Q0]), "cplaneType" : CPlaneType.OFFSET, "offset" : 0 * mm, "width" : 150 * mm, "height" : 150 * mm});
        }
        {
            var Q0;
            Q0=qCreatedBy(id+"F23.planeOp",FACE);
            var sketch = newSketch(context, id + "F24", { "sketchPlane" : qUnion([Q0])});
            skLineSegment(sketch, "E164", {"start": v(-87, -3.82) * mm, "end": v(-87, -3.82) * mm});
            skLineSegment(sketch, "E165", {"start": v(-41.5, -10) * mm, "end": v(-41.5, -20) * mm});
            skLineSegment(sketch, "E166", {"start": v(41.5, -20) * mm, "end": v(41.5, -10) * mm});
            skPoint(sketch, "E167.visualSharp", {"position": v(-41.5, -5) * mm});
            skArc(sketch, "E167.filletArc", {"start": v(-36.5, -5) * mm, "mid": v(-40.04, -6.46) * mm, "end": v(-41.5, -10) * mm});
            skPoint(sketch, "E168.visualSharp", {"position": v(-41.5, -25) * mm});
            skArc(sketch, "E168.filletArc", {"start": v(-41.5, -20) * mm, "mid": v(-40.04, -23.54) * mm, "end": v(-36.5, -25) * mm});
            skPoint(sketch, "E169.visualSharp", {"position": v(41.5, -5) * mm});
            skArc(sketch, "E169.filletArc", {"start": v(41.5, -10) * mm, "mid": v(40.04, -6.46) * mm, "end": v(36.5, -5) * mm});
            skPoint(sketch, "E170.visualSharp", {"position": v(41.5, -25) * mm});
            skArc(sketch, "E170.filletArc", {"start": v(36.5, -25) * mm, "mid": v(40.04, -23.54) * mm, "end": v(41.5, -20) * mm});
            skLineSegment(sketch, "E171.MirrorCS", {"start": v(33.5, -25) * mm, "end": v(36.5, -25) * mm});
            skLineSegment(sketch, "E172.MirrorCS", {"start": v(-36.5, -25) * mm, "end": v(-33.5, -25) * mm});
            skLineSegment(sketch, "E173.MirrorCS", {"start": v(-1.5, -25) * mm, "end": v(1.5, -25) * mm});
            skPoint(sketch, "E174.0", {"position": v(33.5, -25) * mm});
            skPoint(sketch, "E175.0", {"position": v(-36.5, -25) * mm});
            skPoint(sketch, "E176.orphan", {"position": v(36.5, -15) * mm});
            skPoint(sketch, "E177.end.orphan", {"position": v(-36.5, -15) * mm});
            skLineSegment(sketch, "E178", {"start": v(33.5, -5) * mm, "end": v(1.5, -5) * mm});
            skLineSegment(sketch, "E179.MirrorCS", {"start": v(-1.5, -5) * mm, "end": v(-1.5, -15) * mm});
            skLineSegment(sketch, "E180.MirrorCS", {"start": v(1.5, -15) * mm, "end": v(1.5, -5) * mm});
            skLineSegment(sketch, "E181.MirrorCS", {"start": v(-33.5, -15) * mm, "end": v(-33.5, -5) * mm});
            skLineSegment(sketch, "E182.MirrorCS", {"start": v(-36.5, -5) * mm, "end": v(-36.5, -15) * mm});
            skLineSegment(sketch, "E183.MirrorCS", {"start": v(33.5, -5) * mm, "end": v(33.5, -15) * mm});
            skLineSegment(sketch, "E184.MirrorCS", {"start": v(36.5, -15) * mm, "end": v(36.5, -5) * mm});
            skPoint(sketch, "E185.MirrorCS.start.orphan", {"position": v(-36.5, -35) * mm});
            skLineSegment(sketch, "E186.trimOffspring", {"start": v(-1.5, -5) * mm, "end": v(-33.5, -5) * mm});
            skLineSegment(sketch, "E187", {"start": v(-36.5, -25) * mm, "end": v(36.5, -25) * mm});
            skLineSegment(sketch, "E188", {"start": v(-36.5, -15) * mm, "end": v(-33.5, -15) * mm});
            skLineSegment(sketch, "E189", {"start": v(36.5, -15) * mm, "end": v(33.5, -15) * mm});
            skLineSegment(sketch, "E190", {"start": v(1.5, -15) * mm, "end": v(-1.5, -15) * mm});
            skSolve(sketch);
        }
        {
            var Q0;
            Q0 = qSketchRegion(id + "F24", true);
            extrude(context, id + "F25", {"entities" : qUnion([Q0]), "depth" : 3 * mm, "offsetDistance" : 25 * mm});
        }
        {
            var Q0;
            Q0=makeQuery(id+"F4.opExtrude","CAP_FACE",FACE,{"disambiguationData":[OSD([sQuery(id+"F3.wireOp",EDGE,"E5.bottom"),sQuery(id+"F3.wireOp",EDGE,"E5.top"),sQuery(id+"F3.wireOp",EDGE,"E5.left"),sQuery(id+"F3.wireOp",EDGE,"E5.right"),sQuery(id+"F3.wireOp",EDGE,"E6.filletArc"),sQuery(id+"F3.wireOp",EDGE,"E7.filletArc"),sQuery(id+"F3.wireOp",EDGE,"E8.filletArc"),sQuery(id+"F3.wireOp",EDGE,"E9.filletArc"),sQuery(id+"F3.wireOp",EDGE,"E10.bottom"),sQuery(id+"F3.wireOp",EDGE,"E10.top"),sQuery(id+"F3.wireOp",EDGE,"E10.left"),sQuery(id+"F3.wireOp",EDGE,"E10.right"),sQuery(id+"F3.wireOp",EDGE,"E11"),sQuery(id+"F3.wireOp",EDGE,"E15.MirrorC"),sQuery(id+"F3.wireOp",EDGE,"E17.MirrorC"),sQuery(id+"F3.wireOp",EDGE,"E18.MirrorC")])],"isStart":false});
            var sketch = newSketch(context, id + "F26", { "sketchPlane" : qUnion([Q0])});
            skArc(sketch, "E191.0", {"start": v(-79, -100) * mm, "mid": v(-76.07, -107.07) * mm, "end": v(-69, -110) * mm});
            skLineSegment(sketch, "E192", {"start": v(-79, -100) * mm, "end": v(-79, -72.5) * mm});
            skLineSegment(sketch, "E193", {"start": v(-74, -67.5) * mm, "end": v(-66.5, -67.5) * mm});
            skLineSegment(sketch, "E194", {"start": v(-61.5, -72.5) * mm, "end": v(-61.5, -92.5) * mm});
            skPoint(sketch, "E195.0.2.start.orphan", {"position": v(-61.5, -92.5) * mm});
            skLineSegment(sketch, "E196", {"start": v(-69, -110) * mm, "end": v(-41.5, -110) * mm});
            skLineSegment(sketch, "E197", {"start": v(-36.5, -105) * mm, "end": v(-36.5, -97.5) * mm});
            skLineSegment(sketch, "E198", {"start": v(-41.5, -92.5) * mm, "end": v(-61.5, -92.5) * mm});
            skPoint(sketch, "E199.visualSharp", {"position": v(-79, -67.5) * mm});
            skArc(sketch, "E199.filletArc", {"start": v(-74, -67.5) * mm, "mid": v(-77.54, -68.96) * mm, "end": v(-79, -72.5) * mm});
            skPoint(sketch, "E200.visualSharp", {"position": v(-61.5, -67.5) * mm});
            skArc(sketch, "E200.filletArc", {"start": v(-61.5, -72.5) * mm, "mid": v(-62.96, -68.96) * mm, "end": v(-66.5, -67.5) * mm});
            skPoint(sketch, "E201.visualSharp", {"position": v(-36.5, -92.5) * mm});
            skArc(sketch, "E201.filletArc", {"start": v(-36.5, -97.5) * mm, "mid": v(-37.96, -93.96) * mm, "end": v(-41.5, -92.5) * mm});
            skPoint(sketch, "E202.visualSharp", {"position": v(-36.5, -110) * mm});
            skArc(sketch, "E202.filletArc", {"start": v(-41.5, -110) * mm, "mid": v(-37.96, -108.54) * mm, "end": v(-36.5, -105) * mm});
            skLineSegment(sketch, "E203.MirrorCS", {"start": v(41.5, -92.5) * mm, "end": v(61.5, -92.5) * mm});
            skArc(sketch, "E204.MirrorCS", {"start": v(74, -67.5) * mm, "mid": v(77.54, -68.96) * mm, "end": v(79, -72.5) * mm});
            skArc(sketch, "E205.MirrorCS", {"start": v(41.5, -110) * mm, "mid": v(37.96, -108.54) * mm, "end": v(36.5, -105) * mm});
            skArc(sketch, "E206.MirrorCS", {"start": v(36.5, -97.5) * mm, "mid": v(37.96, -93.96) * mm, "end": v(41.5, -92.5) * mm});
            skLineSegment(sketch, "E207.MirrorCS", {"start": v(36.5, -105) * mm, "end": v(36.5, -97.5) * mm});
            skLineSegment(sketch, "E208.MirrorCS", {"start": v(61.5, -72.5) * mm, "end": v(61.5, -92.5) * mm});
            skArc(sketch, "E209.MirrorCS", {"start": v(61.5, -72.5) * mm, "mid": v(62.96, -68.96) * mm, "end": v(66.5, -67.5) * mm});
            skLineSegment(sketch, "E210.MirrorCS", {"start": v(74, -67.5) * mm, "end": v(66.5, -67.5) * mm});
            skPoint(sketch, "E211.MirrorP", {"position": v(79, -67.5) * mm});
            skArc(sketch, "E212.MirrorCS", {"start": v(79, -100) * mm, "mid": v(76.07, -107.07) * mm, "end": v(69, -110) * mm});
            skLineSegment(sketch, "E213.MirrorCS", {"start": v(79, -100) * mm, "end": v(79, -72.5) * mm});
            skPoint(sketch, "E214.MirrorP", {"position": v(61.5, -67.5) * mm});
            skLineSegment(sketch, "E215.MirrorCS", {"start": v(69, -110) * mm, "end": v(41.5, -110) * mm});
            skPoint(sketch, "E216.MirrorP", {"position": v(61.5, -92.5) * mm});
            skPoint(sketch, "E217.MirrorP", {"position": v(36.5, -110) * mm});
            skPoint(sketch, "E218.MirrorP", {"position": v(36.5, -92.5) * mm});
            skLineSegment(sketch, "E219.MirrorCS", {"start": v(-36.5, 105) * mm, "end": v(-36.5, 97.5) * mm});
            skLineSegment(sketch, "E220.MirrorCS", {"start": v(41.5, 92.5) * mm, "end": v(61.5, 92.5) * mm});
            skArc(sketch, "E221.MirrorCS", {"start": v(-41.5, 110) * mm, "mid": v(-37.96, 108.54) * mm, "end": v(-36.5, 105) * mm});
            skArc(sketch, "E222.MirrorCS", {"start": v(-74, 67.5) * mm, "mid": v(-77.54, 68.96) * mm, "end": v(-79, 72.5) * mm});
            skLineSegment(sketch, "E223.MirrorCS", {"start": v(-41.5, 92.5) * mm, "end": v(-61.5, 92.5) * mm});
            skArc(sketch, "E224.MirrorCS", {"start": v(-36.5, 97.5) * mm, "mid": v(-37.96, 93.96) * mm, "end": v(-41.5, 92.5) * mm});
            skLineSegment(sketch, "E225.MirrorCS", {"start": v(-74, 67.5) * mm, "end": v(-66.5, 67.5) * mm});
            skLineSegment(sketch, "E226.MirrorCS", {"start": v(-61.5, 72.5) * mm, "end": v(-61.5, 92.5) * mm});
            skArc(sketch, "E227.MirrorCS", {"start": v(-61.5, 72.5) * mm, "mid": v(-62.96, 68.96) * mm, "end": v(-66.5, 67.5) * mm});
            skArc(sketch, "E228.MirrorCS", {"start": v(79, 100) * mm, "mid": v(76.07, 107.07) * mm, "end": v(69, 110) * mm});
            skLineSegment(sketch, "E229.MirrorCS", {"start": v(36.5, 105) * mm, "end": v(36.5, 97.5) * mm});
            skLineSegment(sketch, "E230.MirrorCS", {"start": v(69, 110) * mm, "end": v(41.5, 110) * mm});
            skLineSegment(sketch, "E231.MirrorCS", {"start": v(61.5, 72.5) * mm, "end": v(61.5, 92.5) * mm});
            skLineSegment(sketch, "E232.MirrorCS", {"start": v(-79, 100) * mm, "end": v(-79, 72.5) * mm});
            skArc(sketch, "E233.MirrorCS", {"start": v(61.5, 72.5) * mm, "mid": v(62.96, 68.96) * mm, "end": v(66.5, 67.5) * mm});
            skLineSegment(sketch, "E234.MirrorCS", {"start": v(-69, 110) * mm, "end": v(-41.5, 110) * mm});
            skArc(sketch, "E235.MirrorCS", {"start": v(74, 67.5) * mm, "mid": v(77.54, 68.96) * mm, "end": v(79, 72.5) * mm});
            skArc(sketch, "E236.MirrorCS", {"start": v(-79, 100) * mm, "mid": v(-76.07, 107.07) * mm, "end": v(-69, 110) * mm});
            skPoint(sketch, "E237.MirrorP", {"position": v(61.5, 92.5) * mm});
            skLineSegment(sketch, "E238.MirrorCS", {"start": v(74, 67.5) * mm, "end": v(66.5, 67.5) * mm});
            skArc(sketch, "E239.MirrorCS", {"start": v(36.5, 97.5) * mm, "mid": v(37.96, 93.96) * mm, "end": v(41.5, 92.5) * mm});
            skArc(sketch, "E240.MirrorCS", {"start": v(41.5, 110) * mm, "mid": v(37.96, 108.54) * mm, "end": v(36.5, 105) * mm});
            skLineSegment(sketch, "E241.MirrorCS", {"start": v(79, 100) * mm, "end": v(79, 72.5) * mm});
            skPoint(sketch, "E242.MirrorP", {"position": v(-61.5, 67.5) * mm});
            skPoint(sketch, "E243.MirrorP", {"position": v(61.5, 67.5) * mm});
            skPoint(sketch, "E244.MirrorP", {"position": v(79, 67.5) * mm});
            skPoint(sketch, "E245.MirrorP", {"position": v(-36.5, 110) * mm});
            skPoint(sketch, "E246.MirrorP", {"position": v(-36.5, 92.5) * mm});
            skPoint(sketch, "E247.MirrorP", {"position": v(-79, 67.5) * mm});
            skPoint(sketch, "E248.MirrorP", {"position": v(-61.5, 92.5) * mm});
            skPoint(sketch, "E249.MirrorP", {"position": v(36.5, 110) * mm});
            skPoint(sketch, "E250.MirrorP", {"position": v(36.5, 92.5) * mm});
            skSolve(sketch);
        }
        {
            var Q0;
            Q0 = qSketchRegion(id + "F26", true);
            extrude(context, id + "F27", {"entities" : qUnion([Q0]), "depth" : 3 * mm, "offsetDistance" : 25 * mm});
        }
    });
